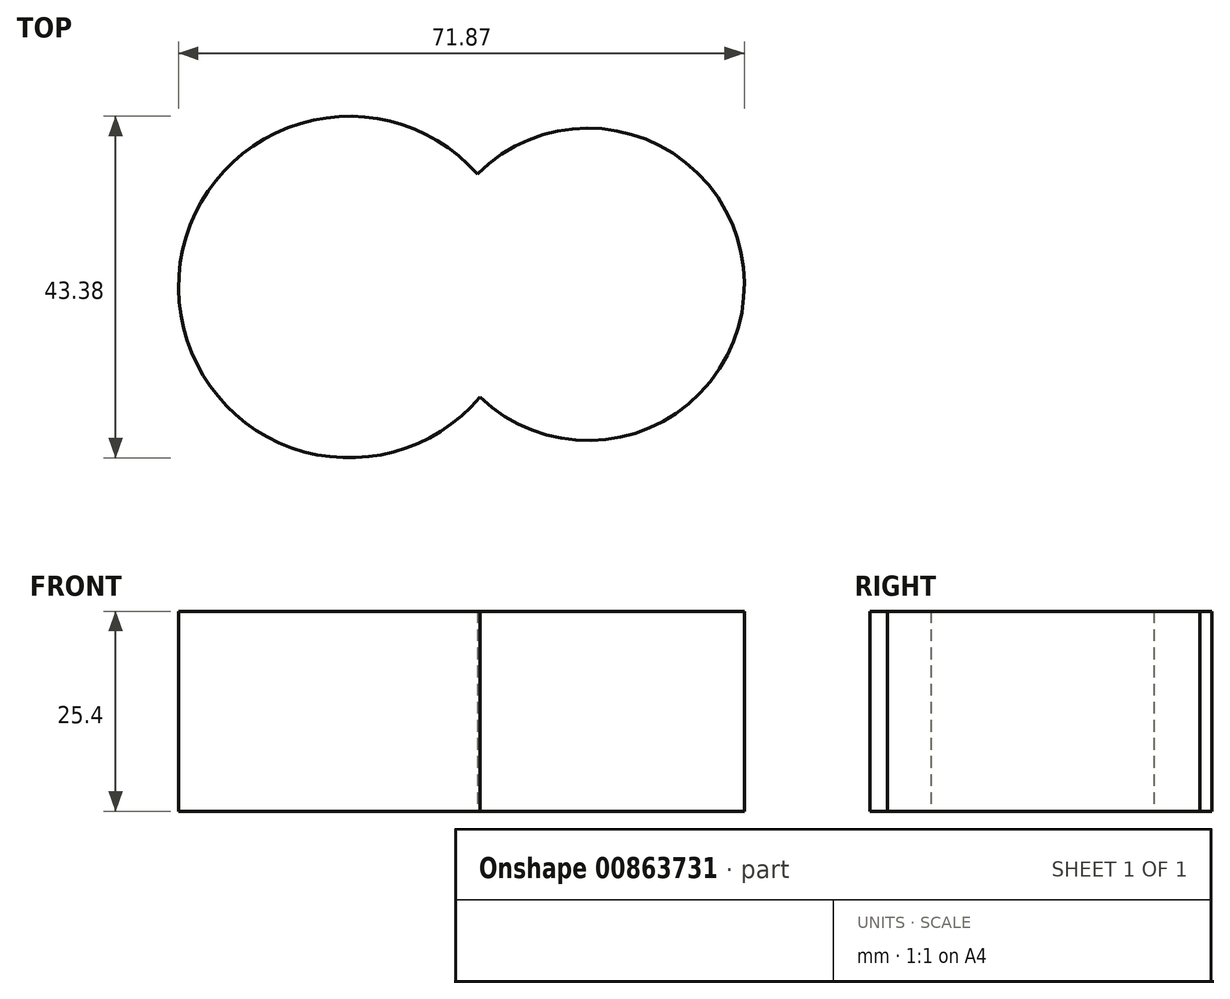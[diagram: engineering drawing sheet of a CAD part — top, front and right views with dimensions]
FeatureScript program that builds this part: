
annotation { "Feature Type Name" : "Feature", "Feature Type Description" : "" }
export const myFeature = defineFeature(function(context is Context, id is Id, definition is map)
    precondition{}
    {
        {
            var Q0;
            Q0=qCreatedBy(makeId("Top.planeOp"),FACE);
            var sketch = newSketch(context, id + "F0", { "sketchPlane" : qUnion([Q0])});
            skLineSegment(sketch, "E0", {"start": v(37.1, 0.79) * mm, "end": v(37.85, 0) * mm});
            skArc(sketch, "E1", {"start": v(-0.76, 11.65) * mm, "mid": v(32.82, 26.18) * mm, "end": v(-1.08, 39.96) * mm});
            skArc(sketch, "E2", {"start": v(-0.35, 39.08) * mm, "mid": v(-39.04, 25.95) * mm, "end": v(-0.76, 11.65) * mm});
            skLineSegment(sketch, "E3.trimOffspring", {"start": v(-0.35, 39.08) * mm, "end": v(0, 39.5) * mm});
            skPoint(sketch, "E4.end.orphan", {"position": v(0, -28.49) * mm});
            skPoint(sketch, "E5.end.orphan", {"position": v(-31.94, 0) * mm});
            skLineSegment(sketch, "E6", {"start": v(-38.98, 23.92) * mm, "end": v(0, -28.49) * mm});
            skLineSegment(sketch, "E7", {"start": v(32.35, 21.67) * mm, "end": v(0, -27.04) * mm});
            skSolve(sketch);
        }
        {
            var Q0;
            Q0 = qSketchRegion(id + "F0", true);
            extrude(context, id + "F1", {"entities" : qUnion([Q0]), "depth" : 25.4 * mm, "offsetDistance" : 25.4 * mm});
        }
    });
